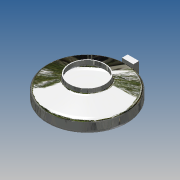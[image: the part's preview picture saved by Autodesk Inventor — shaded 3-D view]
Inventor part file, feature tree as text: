
AUTODESK INVENTOR PART (.ipt)
format: ipt  version: 2014 SP1 (Build 180222100, 222)  size: 224,256 bytes
history: native  units: in
note: dims shown in document units (in); Inventor stores cm internally (conversion verified against a paired STEP export)
features: sketch x2, revolve x1, extrude x1, other x1
ambient origin geometry x8: Origin, YZ Plane, XZ Plane, XY Plane, X Axis, Y Axis, Z Axis, Center Point
bodies: Solid1 (feature_tree)
feature tree (5):
  revolve  "Revolution1"  [1 undecoded]
  extrude  "Extrusion1"  Depth=2.0in
  other  "Power"
  sketch  "Sketch1"  dims[d0=1.0in d1=4.0in]
  sketch  "Sketch3"  dims[d2=0.6528in d3=2.0in d4=0.6528in d7=0.5in d9=1.0in d10=0.5in d11=0.15in d12=3.0in d13=90.0deg d14=2.0in d15=1.0in d16=2.0in d17=0.0in]
note: 1 required parameter value undecoded (feature->parameter linkage not recoverable at this tier; creation-order binding heuristic only, values carry confidence <= 0.55)
